# Revit family: Site-Waste_Management-EarthBin-EB260-bk1
name_source: partatom
category: Site
units: mm (PartAtom-declared; Revit-internal decimal feet)

## family parameters
Always vertical = Yes
Cut with Voids When Loaded = No
OmniClass Number = 23.70.30.21.14
OmniClass Title = Solid Waste Bins
Part Type = Normal
Round Connector Dimension = Use Diameter
Shared = No
Work Plane-Based = No

## types (2) — shared parameters
Assembly Code = E1090200
CD_Depth = 5' - 10"
CD_Feed Height = 3' - 9 1/4"
CD_Finish Feed Door = Plastic-Polyethylene-EarthBin-Feed_Door-Green
CD_Finish Frame = Metal-Steel-EarthBin
CD_Finish Lid = Plastic-Polyethylene-EarthBin-Lid-Grey
CD_Height = 4' - 3 1/4"
CD_Microsite = https://www.caddetails.com
CD_Product Documentation Link = https://static1.squarespace.com
CD_Product Name = Front Load On Ground EB260
CD_Product Page URL = https://www.earthbin.com
CD_Specification = https://www.earthbin.com
CD_Width = 6' - 8"
Default Elevation = 0' - 0"
Description = Rectangular waste & recycling
Manufacturer = EarthBin
Model = EB260
Type Comments = 4.0 cu. yd. (3000 litres)
URL = https://www.earthbin.com

## per-type parameters (varying)
| type | CD_Finish Bin |
| Brown | Plastic-Polyethylene-EarthBin-Panel_Wide-Brown |
| Black | Plastic-Polyethylene-EarthBin-Panel_Wide-Black |

## geometry (parser evidence)
native form markers: Sweep x8
no freeform markers — native parametric forms only
